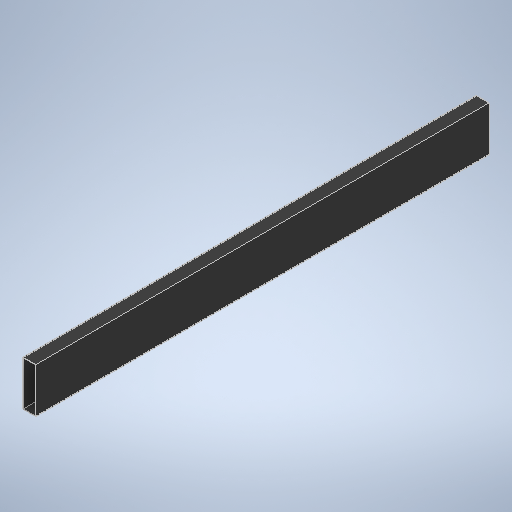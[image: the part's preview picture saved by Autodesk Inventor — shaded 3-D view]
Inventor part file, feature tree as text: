
AUTODESK INVENTOR PART (.ipt)
format: ipt  version: 2025 (Build 290162010, 162A)  size: 258,560 bytes
history: native  units: in
note: dims shown in document units (in); Inventor stores cm internally (conversion verified against a paired STEP export)
features: extrude x1, sketch x1
ambient origin geometry x8: Origin, YZ Plane, XZ Plane, XY Plane, X Axis, Y Axis, Z Axis, Center Point
bodies: Solid1 (feature_tree)
feature tree (2):
  extrude  "Extrusion1"  Depth=1.5in
  sketch  "Sketch1"  dims[d1=5.5in d2=1.5in d3=0.0625in d4=56.5625in d5=0.0in]
